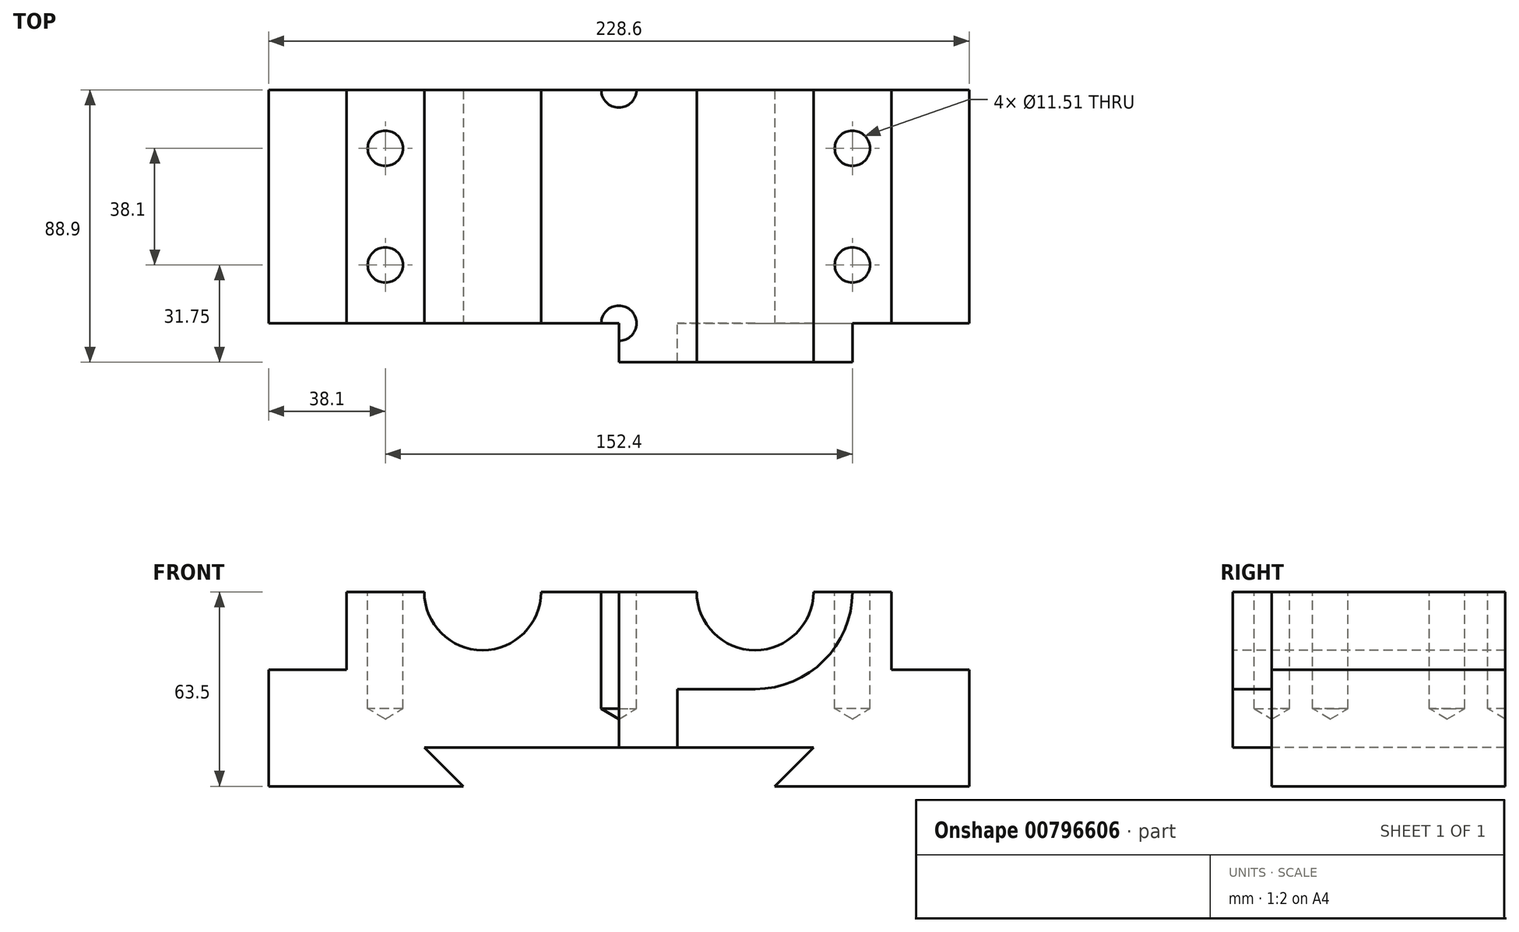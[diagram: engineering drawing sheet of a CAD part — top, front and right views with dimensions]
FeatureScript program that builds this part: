
annotation { "Feature Type Name" : "Feature", "Feature Type Description" : "" }
export const myFeature = defineFeature(function(context is Context, id is Id, definition is map)
    precondition{}
    {
        {
            var Q0;
            Q0=qCreatedBy(makeId("Front.planeOp"),FACE);
            var sketch = newSketch(context, id + "F0", { "sketchPlane" : qUnion([Q0])});
            skLineSegment(sketch, "E0", {"start": v(-114.3, 0) * mm, "end": v(114.3, 0) * mm});
            skLineSegment(sketch, "E1", {"start": v(114.3, 0) * mm, "end": v(114.3, 38.1) * mm});
            skLineSegment(sketch, "E2", {"start": v(114.3, 38.1) * mm, "end": v(88.9, 38.1) * mm});
            skLineSegment(sketch, "E3", {"start": v(88.9, 38.1) * mm, "end": v(88.9, 63.5) * mm});
            skLineSegment(sketch, "E4", {"start": v(88.9, 63.5) * mm, "end": v(-88.9, 63.5) * mm});
            skLineSegment(sketch, "E5", {"start": v(-88.9, 63.5) * mm, "end": v(-88.9, 38.1) * mm});
            skLineSegment(sketch, "E6", {"start": v(-88.9, 38.1) * mm, "end": v(-114.3, 38.1) * mm});
            skLineSegment(sketch, "E7", {"start": v(-114.3, 38.1) * mm, "end": v(-114.3, 0) * mm});
            skSolve(sketch);
        }
        {
            var Q0;
            Q0 = qSketchRegion(id + "F0", true);
            extrude(context, id + "F1", {"entities" : qUnion([Q0]), "endBound" : BoundingType.SYMMETRIC, "depth" : 76.2 * mm, "offsetDistance" : 25.4 * mm});
        }
        {
            var Q0;
            Q0=makeQuery(id+"F1.opExtrude","CAP_FACE",FACE,{"disambiguationData":[OSD([sQuery(id+"F0.wireOp",EDGE,"E0"),sQuery(id+"F0.wireOp",EDGE,"E1"),sQuery(id+"F0.wireOp",EDGE,"E2"),sQuery(id+"F0.wireOp",EDGE,"E3"),sQuery(id+"F0.wireOp",EDGE,"E4"),sQuery(id+"F0.wireOp",EDGE,"E5"),sQuery(id+"F0.wireOp",EDGE,"E6"),sQuery(id+"F0.wireOp",EDGE,"E7")])],"isStart":false});
            var sketch = newSketch(context, id + "F2", { "sketchPlane" : qUnion([Q0])});
            skArc(sketch, "E8", {"start": v(44.45, 31.75) * mm, "mid": v(66.9, 41.05) * mm, "end": v(76.2, 63.5) * mm});
            skLineSegment(sketch, "E9", {"start": v(44.45, 31.75) * mm, "end": v(19.05, 31.75) * mm});
            skLineSegment(sketch, "E10", {"start": v(19.05, 31.75) * mm, "end": v(19.05, 0) * mm});
            skLineSegment(sketch, "E11", {"start": v(76.2, 63.5) * mm, "end": v(0, 63.5) * mm});
            skLineSegment(sketch, "E12", {"start": v(0, 63.5) * mm, "end": v(0, 0) * mm});
            skLineSegment(sketch, "E13", {"start": v(0, 0) * mm, "end": v(19.05, 0) * mm});
            skSolve(sketch);
        }
        {
            var Q0;
            Q0 = qSketchRegion(id + "F2", true);
            extrude(context, id + "F3", {"entities" : qUnion([Q0]), "operationType" : NewBodyOperationType.ADD, "depth" : 12.7 * mm, "offsetDistance" : 25.4 * mm});
        }
        {
            var Q0;
            {var subQ0=sQuery(id+"F2.wireOp",EDGE,"E13");var subQ1=sQuery(id+"F2.wireOp",EDGE,"E12");var subQ2=sQuery(id+"F2.wireOp",EDGE,"E11");var subQ3=sQuery(id+"F2.wireOp",EDGE,"E10");var subQ4=sQuery(id+"F2.wireOp",EDGE,"E9");var subQ5=sQuery(id+"F2.wireOp",EDGE,"E8");Q0=makeQuery(id+"FEUMpz2HPAO64D4_1.1.F3.boolean.opBoolean","MERGE",FACE,{"derivedFrom":[makeQuery(id+"F3.opExtrude","CAP_FACE",FACE,{"disambiguationData":[OSD([subQ5,subQ4,subQ3,subQ2,subQ1,subQ0])],"isStart":false}),makeQuery(id+"FEUMpz2HPAO64D4_1.1.F3.opExtrude","CAP_FACE",FACE,{"disambiguationData":[OSD([subQ5,subQ4,subQ3,subQ2,subQ1,subQ0])],"isStart":false})]});}
            var sketch = newSketch(context, id + "F4", { "sketchPlane" : qUnion([Q0])});
            skLineSegment(sketch, "E14", {"start": v(-50.8, 0) * mm, "end": v(-63.5, 12.7) * mm});
            skLineSegment(sketch, "E15", {"start": v(-63.5, 12.7) * mm, "end": v(63.5, 12.7) * mm});
            skLineSegment(sketch, "E16", {"start": v(63.5, 12.7) * mm, "end": v(50.8, 0) * mm});
            skLineSegment(sketch, "E17", {"start": v(50.8, 0) * mm, "end": v(-50.8, 0) * mm});
            skSolve(sketch);
        }
        {
            var Q0;
            Q0 = qSketchRegion(id + "F4", true);
            extrude(context, id + "F5", {"entities" : qUnion([Q0]), "operationType" : NewBodyOperationType.REMOVE, "endBound" : BoundingType.THROUGH_ALL, "oppositeDirection" : true, "depth" : 25.4 * mm, "offsetDistance" : 25.4 * mm});
        }
        {
            var Q0;
            {var subQ0=sQuery(id+"F2.wireOp",EDGE,"E11");Q0=makeQuery(id+"FrLiCTJj3pnx7B2_1.1.FEUMpz2HPAO64D4_1.1.F3.boolean.opBoolean","MERGE",FACE,{"derivedFrom":[makeQuery(id+"FrLiCTJj3pnx7B2_1.1.F3.boolean.opBoolean","MERGE",FACE,{"derivedFrom":[makeQuery(id+"FEUMpz2HPAO64D4_1.1.F3.boolean.opBoolean","MERGE",FACE,{"derivedFrom":[makeQuery(id+"F3.boolean.opBoolean","MERGE",FACE,{"derivedFrom":[makeQuery(id+"F1.opExtrude","SWEPT_FACE",FACE,{"disambiguationData":[OSD([sQuery(id+"F0.wireOp",EDGE,"E4")])]}),makeQuery(id+"F3.opExtrude","SWEPT_FACE",FACE,{"disambiguationData":[OSD([subQ0])]})]}),makeQuery(id+"FEUMpz2HPAO64D4_1.1.F3.opExtrude","SWEPT_FACE",FACE,{"disambiguationData":[OSD([subQ0])]})]}),makeQuery(id+"FrLiCTJj3pnx7B2_1.1.F3.opExtrude","SWEPT_FACE",FACE,{"disambiguationData":[OSD([subQ0])]})]}),makeQuery(id+"FrLiCTJj3pnx7B2_1.1.FEUMpz2HPAO64D4_1.1.F3.opExtrude","SWEPT_FACE",FACE,{"disambiguationData":[OSD([subQ0])]})]});}
            var sketch = newSketch(context, id + "F6", { "sketchPlane" : qUnion([Q0])});
            skPoint(sketch, "E18", {"position": v(-76.2, -19.05) * mm});
            skPoint(sketch, "E19", {"position": v(-76.2, 19.05) * mm});
            skPoint(sketch, "E20", {"position": v(0, 38.1) * mm});
            skPoint(sketch, "E21", {"position": v(0, -38.1) * mm});
            skPoint(sketch, "E22", {"position": v(76.2, 19.05) * mm});
            skPoint(sketch, "E23", {"position": v(76.2, -19.05) * mm});
            skSolve(sketch);
        }
        {
            var Q0;
            Q0=sQuery(id+"F6.wireOp",VERTEX,"E19");
            var Q1;
            Q1=sQuery(id+"F6.wireOp",VERTEX,"E18");
            var Q2;
            Q2=sQuery(id+"F6.wireOp",VERTEX,"E20");
            var Q3;
            Q3=sQuery(id+"F6.wireOp",VERTEX,"E21");
            var Q4;
            Q4=sQuery(id+"F6.wireOp",VERTEX,"E23");
            var Q5;
            Q5=sQuery(id+"F6.wireOp",VERTEX,"E22");
            var Q6;
            Q6=makeQuery(id+"F1.opExtrude","SWEPT_BODY",BODY,{"disambiguationData":[OSD([sQuery(id+"F0.wireOp",EDGE,"E0"),sQuery(id+"F0.wireOp",EDGE,"E1"),sQuery(id+"F0.wireOp",EDGE,"E2"),sQuery(id+"F0.wireOp",EDGE,"E3"),sQuery(id+"F0.wireOp",EDGE,"E4"),sQuery(id+"F0.wireOp",EDGE,"E5"),sQuery(id+"F0.wireOp",EDGE,"E6"),sQuery(id+"F0.wireOp",EDGE,"E7")])]});
            hole(context, id + "F7", {"style" : HoleStyle.SIMPLE, "endStyle" : HoleEndStyle.BLIND, "holeDiameter" : 11.5 * mm, "majorDiameter" : 6.35 * mm, "holeDepth" : 38.1 * mm, "isTappedThrough" : true, "tappedDepth" : 12.7 * mm, "tapClearance" : 3, "locations" : qUnion([Q0, Q1, Q2, Q3, Q4, Q5]), "scope" : qUnion([Q6])});
        }
        {
            var Q0;
            {var subQ0=sQuery(id+"F2.wireOp",EDGE,"E13");var subQ1=sQuery(id+"F2.wireOp",EDGE,"E12");var subQ2=sQuery(id+"F2.wireOp",EDGE,"E11");var subQ3=sQuery(id+"F2.wireOp",EDGE,"E10");var subQ4=sQuery(id+"F2.wireOp",EDGE,"E9");var subQ5=sQuery(id+"F2.wireOp",EDGE,"E8");Q0=makeQuery(id+"FEUMpz2HPAO64D4_1.1.F3.boolean.opBoolean","MERGE",FACE,{"derivedFrom":[makeQuery(id+"F3.opExtrude","CAP_FACE",FACE,{"disambiguationData":[OSD([subQ5,subQ4,subQ3,subQ2,subQ1,subQ0])],"isStart":false}),makeQuery(id+"FEUMpz2HPAO64D4_1.1.F3.opExtrude","CAP_FACE",FACE,{"disambiguationData":[OSD([subQ5,subQ4,subQ3,subQ2,subQ1,subQ0])],"isStart":false})]});}
            var sketch = newSketch(context, id + "F8", { "sketchPlane" : qUnion([Q0])});
            skArc(sketch, "E24", {"start": v(-63.5, 63.5) * mm, "mid": v(-44.45, 44.45) * mm, "end": v(-25.4, 63.5) * mm});
            skArc(sketch, "E25", {"start": v(25.4, 63.5) * mm, "mid": v(44.45, 44.45) * mm, "end": v(63.5, 63.5) * mm});
            skLineSegment(sketch, "E26", {"start": v(-63.5, 63.5) * mm, "end": v(-25.4, 63.5) * mm});
            skLineSegment(sketch, "E27", {"start": v(25.4, 63.5) * mm, "end": v(63.5, 63.5) * mm});
            skSolve(sketch);
        }
        {
            var Q0;
            Q0 = qSketchRegion(id + "F8", true);
            extrude(context, id + "F9", {"entities" : qUnion([Q0]), "operationType" : NewBodyOperationType.REMOVE, "endBound" : BoundingType.THROUGH_ALL, "oppositeDirection" : true, "depth" : 25.4 * mm, "offsetDistance" : 25.4 * mm});
        }
    });
